# Revit family: LABELLO Thin Edge Basin Sink
name_source: partatom
category: Generic Models
units: mm (PartAtom-declared; Revit-internal decimal feet)

## family parameters
Always vertical = Yes
Can host rebar = No
Cut with Voids When Loaded = No
Maintain Annotation Orientation = No
OmniClass Number = 23.31.13.11
Part Type = Normal
Room Calculation Point = No
Round Connector Dimension = Use Diameter
Shared = No
Work Plane-Based = No

## types (1)
- LABELLO Thin Edge Basin Sink
    Catalog web link = https://www.abiinteriors.com.au
    Category = Basin Sinks
    Default Elevation = 0 mm  [stored 0 ft]
    Description = LABELLO Thin Edge Basin Sink
    Keywords = Bench Mount, Basin, Sink, Oval
    Manufacturer = ABI Interiors Pty Ltd
    Material = Matte White SB
    Model = Gloss White(15426), Almond(12971), Posy(12972), Matte White(11861)
    Part Number = Gloss White(15426), Almond(12971), Posy(12972), Matte White(11861)
    Title = Labello Basin Sink Thin Edge
    URL = https://www.abiinteriors.com.au
    Volume = 0 m³

note: [stored X ft] marks values corroborated as IEEE doubles in the binary element streams (Revit-internal decimal feet)

## geometry (parser evidence)
native form markers: Sweep x3
no freeform markers — native parametric forms only
